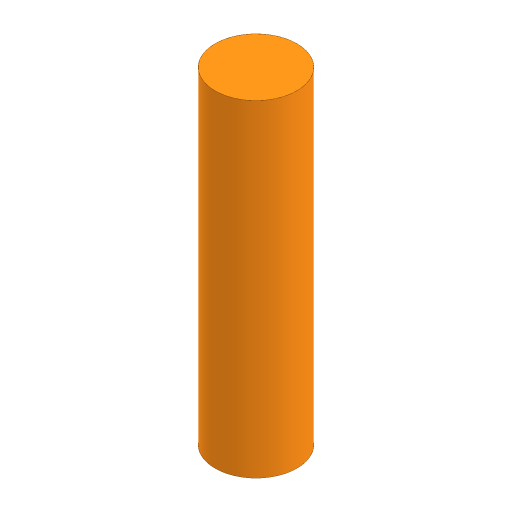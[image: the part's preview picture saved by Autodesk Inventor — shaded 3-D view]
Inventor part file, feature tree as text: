
AUTODESK INVENTOR PART (.ipt)
format: ipt  version: 2023 (Build 270158000, 158)  size: 80,896 bytes
history: native  units: in
note: dims shown in document units (in); Inventor stores cm internally (conversion verified against a paired STEP export)
features: extrude x1, sketch x1
ambient origin geometry x8: Origin, YZ Plane, XZ Plane, XY Plane, X Axis, Y Axis, Z Axis, Center Point
bodies: Solid1 (feature_tree)
feature tree (2):
  extrude  "Extrusion1"  Depth=4.0in TaperAngle=0.0deg
  sketch  "Sketch1"  dims[d0=1.0in d1=4.0in d2=0.0in]
